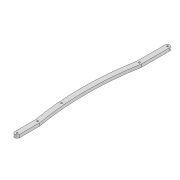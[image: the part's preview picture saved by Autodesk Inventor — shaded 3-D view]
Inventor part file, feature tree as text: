
AUTODESK INVENTOR PART (.ipt)
format: ipt  version: 2022 (Build 260153000, 153)  size: 110,080 bytes
history: native  units: mm
features: extrude x1
ambient origin geometry x8: Origin, YZ Plane, XZ Plane, XY Plane, X Axis, Y Axis, Z Axis, Center Point
bodies: Solid1 (feature_tree)
feature tree (1):
  extrude  "Extrusion1"  Depth=3.3mm
